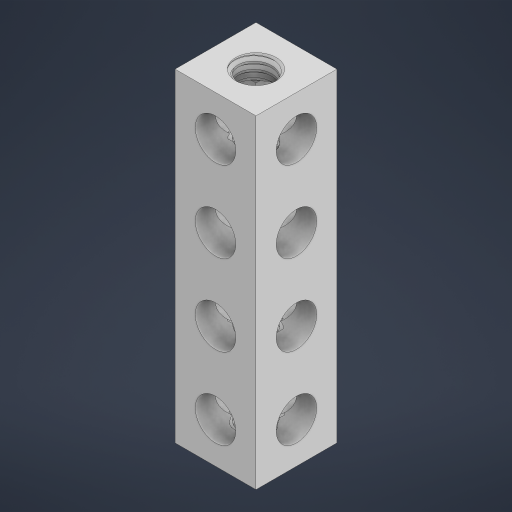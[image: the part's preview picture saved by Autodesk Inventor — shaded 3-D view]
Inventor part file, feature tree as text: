
AUTODESK INVENTOR PART (.ipt)
format: ipt  version: 2023 (Build 270158000, 158)  size: 1,353,216 bytes
history: native  units: in
note: dims shown in document units (in); Inventor stores cm internally (conversion verified against a paired STEP export)
features: mirror x1
ambient origin geometry x8: Origin, YZ Plane, XZ Plane, XY Plane, X Axis, Y Axis, Z Axis, Center Point
bodies: Solid1 (feature_tree)
feature tree (1):
  mirror  "Mirror3"
